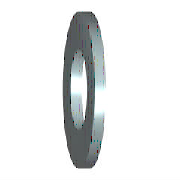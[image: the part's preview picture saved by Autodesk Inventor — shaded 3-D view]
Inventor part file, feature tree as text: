
AUTODESK INVENTOR PART (.ipt)
format: ipt  version: 2023.3 (Build 273359000, 359)  size: 107,520 bytes
history: native  units: mm (DEFAULTED — no unit token found)
features: extrude x1, other x1, plane x1, sketch x1
ambient origin geometry x7: Origin, YZ Plane, XY Plane, X Axis, Y Axis, Z Axis, Center Point
bodies: Solid1 (feature_tree)
feature tree (4):
  extrude  "Körper"  Depth=10.0mm
  other  "Work Axis1"
  plane  "Work Plane1"
  sketch  "Skizze"  dims[d0=5.5mm d1=10.0mm d2=1.0mm d3=0.0mm d4=0.0mm d5=0.0mm d6=0.0mm d7=0.0mm]
